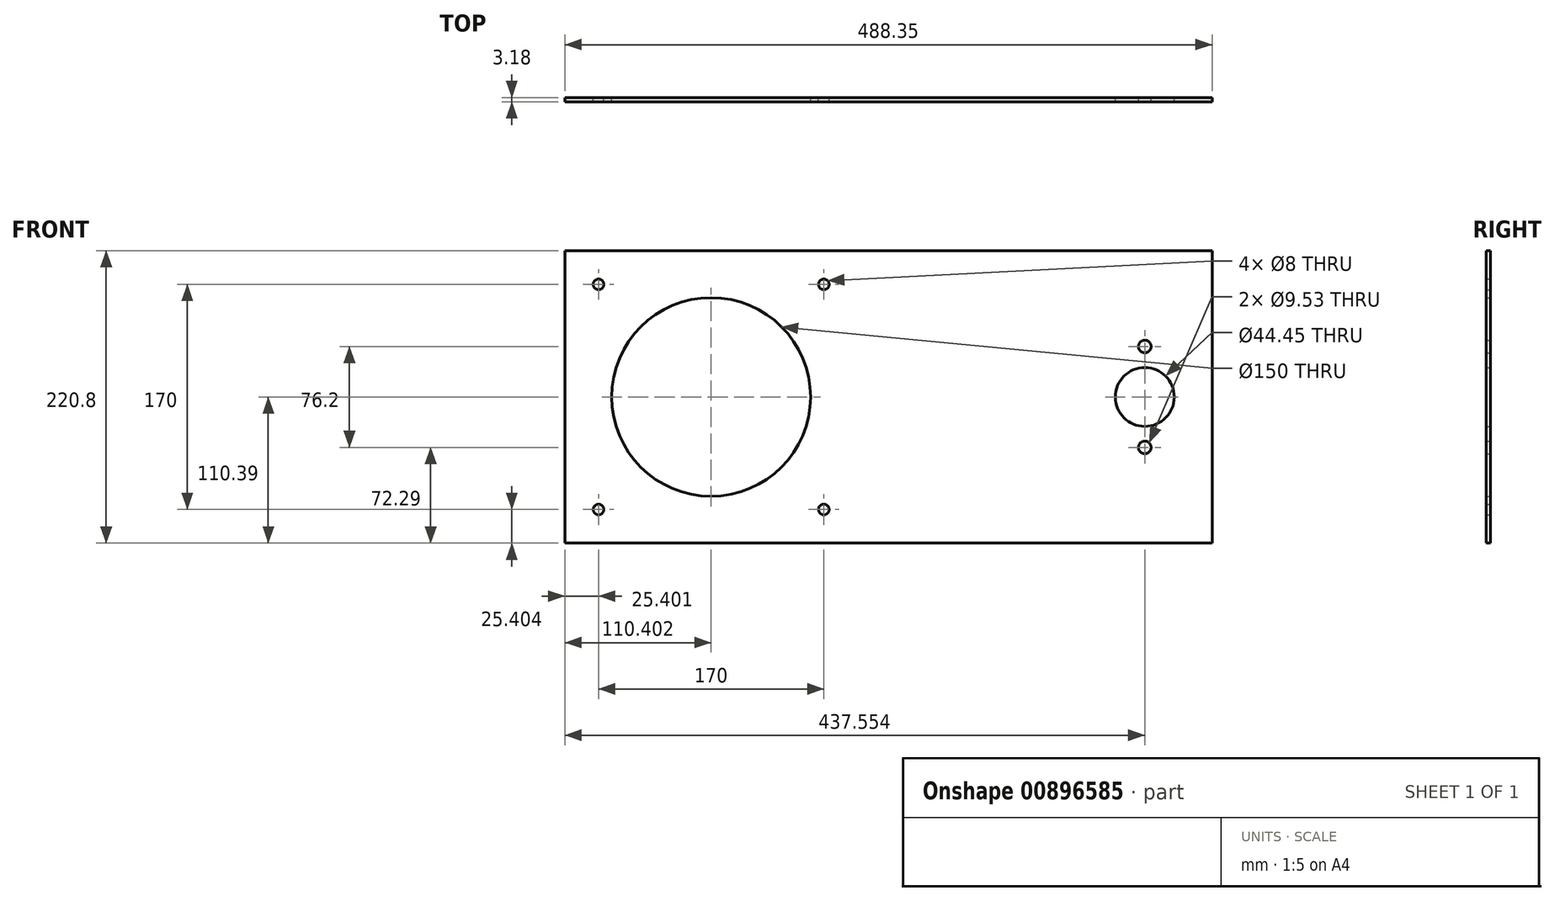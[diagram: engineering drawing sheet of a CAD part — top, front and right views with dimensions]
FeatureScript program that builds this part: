
annotation { "Feature Type Name" : "Feature", "Feature Type Description" : "" }
export const myFeature = defineFeature(function(context is Context, id is Id, definition is map)
    precondition{}
    {
        {
            var Q0;
            Q0=qCreatedBy(makeId("Front.planeOp"),FACE);
            var sketch = newSketch(context, id + "F0", { "sketchPlane" : qUnion([Q0])});
            skCircle(sketch, "E0", {"center": v(-115.44, 123.11) * mm, "radius": 4 * mm});
            skCircle(sketch, "E1", {"center": v(-115.44, -46.89) * mm, "radius": 4 * mm});
            skCircle(sketch, "E2", {"center": v(54.56, -46.89) * mm, "radius": 4 * mm});
            skCircle(sketch, "E3", {"center": v(54.56, 123.11) * mm, "radius": 4 * mm});
            skCircle(sketch, "E4", {"center": v(-30.44, 38.1) * mm, "radius": 75 * mm});
            skLineSegment(sketch, "E5", {"start": v(-140.84, -72.29) * mm, "end": v(-140.84, 148.51) * mm});
            skCircle(sketch, "E6", {"center": v(296.71, 38.1) * mm, "radius": 22.23 * mm});
            skCircle(sketch, "E7", {"center": v(296.71, 76.2) * mm, "radius": 4.76 * mm});
            skCircle(sketch, "E8", {"center": v(296.71, 0) * mm, "radius": 4.76 * mm});
            skLineSegment(sketch, "E9", {"start": v(347.51, 38.1) * mm, "end": v(347.51, 148.51) * mm});
            skLineSegment(sketch, "E10", {"start": v(347.51, 38.1) * mm, "end": v(347.51, -72.29) * mm});
            skLineSegment(sketch, "E11", {"start": v(-140.84, -72.29) * mm, "end": v(347.51, -72.29) * mm});
            skLineSegment(sketch, "E12", {"start": v(-140.84, 148.51) * mm, "end": v(347.51, 148.51) * mm});
            skSolve(sketch);
        }
        {
            var Q0;
            Q0=makeQuery(id+"F0.imprint","IMPRINT",FACE,{"disambiguationData":[TD([[makeQuery(id+"F0.imprint","IMPRINT",EDGE,{"derivedFrom":sQuery(id+"F0.wireOp",EDGE,"E0")}),-1.0]])]});
            extrude(context, id + "F1", {"entities" : qUnion([Q0]), "depth" : 3.17 * mm, "offsetDistance" : 25.4 * mm});
        }
    });
